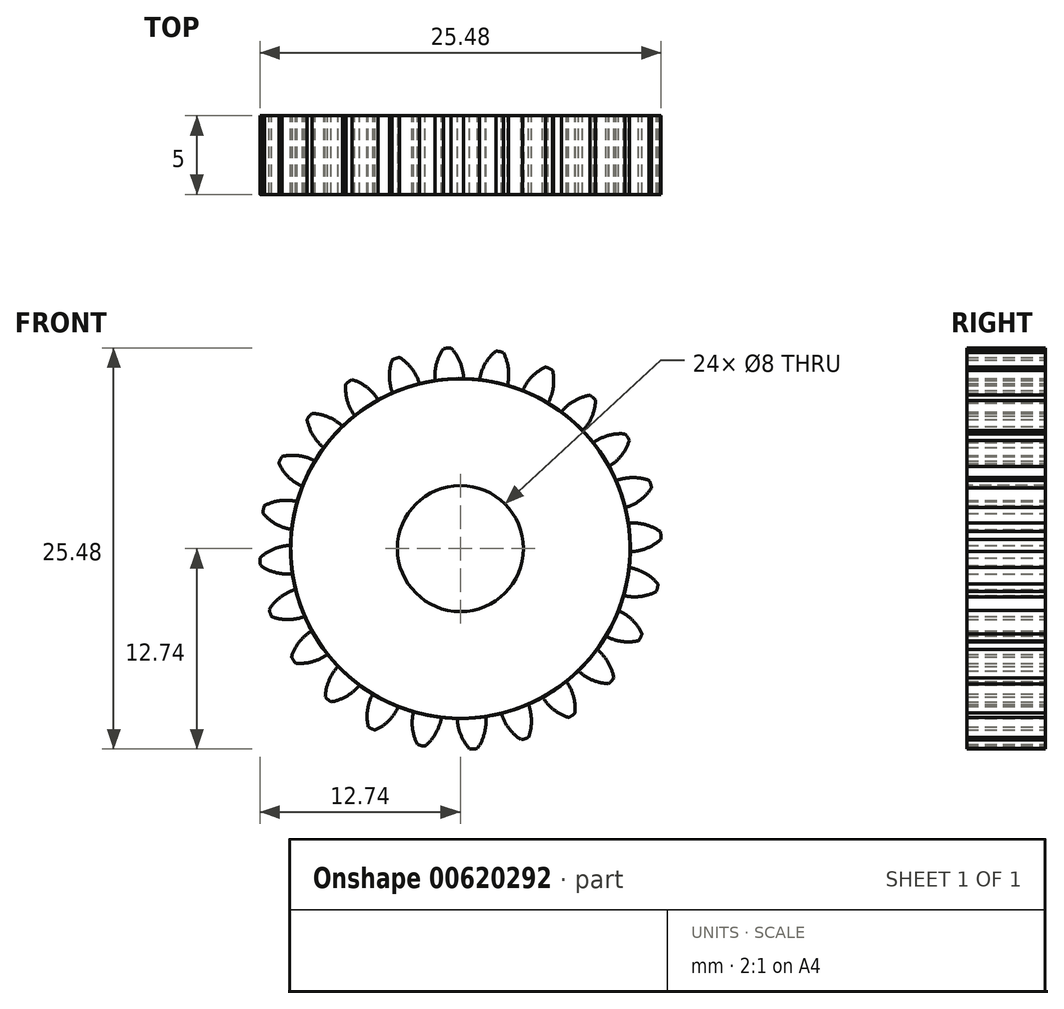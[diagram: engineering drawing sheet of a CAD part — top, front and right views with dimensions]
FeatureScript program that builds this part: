
annotation { "Feature Type Name" : "Feature", "Feature Type Description" : "" }
export const myFeature = defineFeature(function(context is Context, id is Id, definition is map)
    precondition{}
    {
        {
            var Q0;
            Q0=qCreatedBy(makeId("Front.planeOp"),FACE);
            var sketch = newSketch(context, id + "F0", { "sketchPlane" : qUnion([Q0])});
            skCircle(sketch, "E0", {"center": v(0, 0) * mm, "radius": 6.34 * mm});
            skCircle(sketch, "E1", {"center": v(0, 0) * mm, "radius": 6.93 * mm, "construction": true});
            skCircle(sketch, "E2", {"center": v(0, 0) * mm, "radius": 7.5 * mm, "construction": true});
            skLineSegment(sketch, "E3", {"start": v(0, 0) * mm, "end": v(0, 11.09) * mm, "construction": true});
            skLineSegment(sketch, "E4", {"start": v(0, 0) * mm, "end": v(-0.73, 11.09) * mm, "construction": true});
            skLineSegment(sketch, "E5", {"start": v(0, 6.93) * mm, "end": v(-9.56, 6.93) * mm, "construction": true});
            skLineSegment(sketch, "E6", {"start": v(0, 6.93) * mm, "end": v(-10.36, 3.16) * mm, "construction": true});
            skCircle(sketch, "E7", {"center": v(0, 6.93) * mm, "radius": 1.73 * mm, "construction": true});
            skCircle(sketch, "E8", {"center": v(0, 0) * mm, "radius": 6.51 * mm, "construction": true});
            skCircle(sketch, "E9", {"center": v(-1.6, 6.31) * mm, "radius": 1.73 * mm, "construction": true});
            skArc(sketch, "E10", {"start": v(0, 6.93) * mm, "mid": v(-0.15, 7.22) * mm, "end": v(-0.35, 7.49) * mm});
            skArc(sketch, "E11", {"start": v(0.12, 6.34) * mm, "mid": v(0.08, 6.64) * mm, "end": v(0, 6.93) * mm});
            skArc(sketch, "E12.MirrorCS", {"start": v(-0.9, 6.87) * mm, "mid": v(-0.8, 7.18) * mm, "end": v(-0.63, 7.47) * mm});
            skArc(sketch, "E13.MirrorCS", {"start": v(-0.94, 6.27) * mm, "mid": v(-0.95, 6.57) * mm, "end": v(-0.9, 6.87) * mm});
            skArc(sketch, "E14", {"start": v(-0.35, 7.49) * mm, "mid": v(-0.5, 7.5) * mm, "end": v(-0.63, 7.47) * mm});
            skSolve(sketch);
        }
        {
            var Q0;
            {var subQ0=sQuery(id+"F0.wireOp",EDGE,"E0");var subQ1=makeQuery(id+"F0.imprint","INTERSECT",VERTEX,{"derivedFrom":[subQ0,sQuery(id+"F0.wireOp",EDGE,"E11")]});Q0=makeQuery(id+"F0.imprint","IMPRINT",FACE,{"disambiguationData":[TD([[makeQuery(id+"F0.imprint","IMPRINT",EDGE,{"disambiguationData":[TD([[subQ1,-1.0]])],"derivedFrom":subQ0}),1.0]])]});}
            var Q1;
            Q1=makeQuery(id+"F0.imprint","IMPRINT",FACE,{"disambiguationData":[TD([[makeQuery(id+"F0.imprint","IMPRINT",EDGE,{"derivedFrom":sQuery(id+"F0.wireOp",EDGE,"E10")}),1.0]])]});
            extrude(context, id + "F1", {"entities" : qUnion([Q0, Q1]), "depth" : 2.94 * mm, "offsetDistance" : 25 * mm});
        }
        {
            var Q0;
            Q0=makeQuery(id+"F1.opExtrude","SWEPT_BODY",BODY,{"disambiguationData":[OSD([sQuery(id+"F0.wireOp",EDGE,"E0"),sQuery(id+"F0.wireOp",EDGE,"E10"),sQuery(id+"F0.wireOp",EDGE,"E11"),sQuery(id+"F0.wireOp",EDGE,"E12.MirrorCS"),sQuery(id+"F0.wireOp",EDGE,"E13.MirrorCS"),sQuery(id+"F0.wireOp",EDGE,"E14")])]});
            var Q1;
            Q1=makeQuery(id+"F1.opExtrude","SWEPT_FACE",FACE,{"disambiguationData":[OSD([sQuery(id+"F0.wireOp",EDGE,"E0")])]});
            circularPattern(context, id + "F2", {"entities" : qUnion([Q0]), "axis" : qUnion([Q1]), "angle" : 360 * degree, "instanceCount" : 24, "equalSpace" : true});
        }
        {
            var Q0;
            Q0=makeQuery(id+"F2.opPattern","COPY",FACE,{"derivedFrom":makeQuery(id+"F1.opExtrude","CAP_FACE",FACE,{"disambiguationData":[OSD([sQuery(id+"F0.wireOp",EDGE,"E0"),sQuery(id+"F0.wireOp",EDGE,"E10"),sQuery(id+"F0.wireOp",EDGE,"E11"),sQuery(id+"F0.wireOp",EDGE,"E12.MirrorCS"),sQuery(id+"F0.wireOp",EDGE,"E13.MirrorCS"),sQuery(id+"F0.wireOp",EDGE,"E14")])],"isStart":false}),"instanceName":"3"});
            var sketch = newSketch(context, id + "F3", { "sketchPlane" : qUnion([Q0])});
            skCircle(sketch, "E15", {"center": v(0, 0) * mm, "radius": 2.35 * mm});
            skSolve(sketch);
        }
        {
            var Q0;
            Q0=qSketchRegion(id+"F3",true);
            extrude(context, id + "F4", {"entities" : qUnion([Q0]), "operationType" : NewBodyOperationType.REMOVE, "endBound" : BoundingType.UP_TO_NEXT, "oppositeDirection" : true, "depth" : 25 * mm, "offsetDistance" : 25 * mm});
        }
        {
            var Q0;
            Q0=makeQuery(id+"F2.opPattern","COPY",BODY,{"derivedFrom":makeQuery(id+"F1.opExtrude","SWEPT_BODY",BODY,{"disambiguationData":[OSD([sQuery(id+"F0.wireOp",EDGE,"E0"),sQuery(id+"F0.wireOp",EDGE,"E10"),sQuery(id+"F0.wireOp",EDGE,"E11"),sQuery(id+"F0.wireOp",EDGE,"E12.MirrorCS"),sQuery(id+"F0.wireOp",EDGE,"E13.MirrorCS"),sQuery(id+"F0.wireOp",EDGE,"E14")])]}),"instanceName":"23"});
            var Q1;
            Q1=makeQuery(id+"F2.opPattern","COPY",BODY,{"derivedFrom":makeQuery(id+"F1.opExtrude","SWEPT_BODY",BODY,{"disambiguationData":[OSD([sQuery(id+"F0.wireOp",EDGE,"E0"),sQuery(id+"F0.wireOp",EDGE,"E10"),sQuery(id+"F0.wireOp",EDGE,"E11"),sQuery(id+"F0.wireOp",EDGE,"E12.MirrorCS"),sQuery(id+"F0.wireOp",EDGE,"E13.MirrorCS"),sQuery(id+"F0.wireOp",EDGE,"E14")])]}),"instanceName":"11"});
            var Q2;
            Q2=makeQuery(id+"F2.opPattern","COPY",BODY,{"derivedFrom":makeQuery(id+"F1.opExtrude","SWEPT_BODY",BODY,{"disambiguationData":[OSD([sQuery(id+"F0.wireOp",EDGE,"E0"),sQuery(id+"F0.wireOp",EDGE,"E10"),sQuery(id+"F0.wireOp",EDGE,"E11"),sQuery(id+"F0.wireOp",EDGE,"E12.MirrorCS"),sQuery(id+"F0.wireOp",EDGE,"E13.MirrorCS"),sQuery(id+"F0.wireOp",EDGE,"E14")])]}),"instanceName":"12"});
            var Q3;
            Q3=makeQuery(id+"F2.opPattern","COPY",BODY,{"derivedFrom":makeQuery(id+"F1.opExtrude","SWEPT_BODY",BODY,{"disambiguationData":[OSD([sQuery(id+"F0.wireOp",EDGE,"E0"),sQuery(id+"F0.wireOp",EDGE,"E10"),sQuery(id+"F0.wireOp",EDGE,"E11"),sQuery(id+"F0.wireOp",EDGE,"E12.MirrorCS"),sQuery(id+"F0.wireOp",EDGE,"E13.MirrorCS"),sQuery(id+"F0.wireOp",EDGE,"E14")])]}),"instanceName":"3"});
            var Q4;
            Q4=makeQuery(id+"F2.opPattern","COPY",BODY,{"derivedFrom":makeQuery(id+"F1.opExtrude","SWEPT_BODY",BODY,{"disambiguationData":[OSD([sQuery(id+"F0.wireOp",EDGE,"E0"),sQuery(id+"F0.wireOp",EDGE,"E10"),sQuery(id+"F0.wireOp",EDGE,"E11"),sQuery(id+"F0.wireOp",EDGE,"E12.MirrorCS"),sQuery(id+"F0.wireOp",EDGE,"E13.MirrorCS"),sQuery(id+"F0.wireOp",EDGE,"E14")])]}),"instanceName":"13"});
            var Q5;
            Q5=makeQuery(id+"F2.opPattern","COPY",BODY,{"derivedFrom":makeQuery(id+"F1.opExtrude","SWEPT_BODY",BODY,{"disambiguationData":[OSD([sQuery(id+"F0.wireOp",EDGE,"E0"),sQuery(id+"F0.wireOp",EDGE,"E10"),sQuery(id+"F0.wireOp",EDGE,"E11"),sQuery(id+"F0.wireOp",EDGE,"E12.MirrorCS"),sQuery(id+"F0.wireOp",EDGE,"E13.MirrorCS"),sQuery(id+"F0.wireOp",EDGE,"E14")])]}),"instanceName":"7"});
            var Q6;
            Q6=makeQuery(id+"F2.opPattern","COPY",BODY,{"derivedFrom":makeQuery(id+"F1.opExtrude","SWEPT_BODY",BODY,{"disambiguationData":[OSD([sQuery(id+"F0.wireOp",EDGE,"E0"),sQuery(id+"F0.wireOp",EDGE,"E10"),sQuery(id+"F0.wireOp",EDGE,"E11"),sQuery(id+"F0.wireOp",EDGE,"E12.MirrorCS"),sQuery(id+"F0.wireOp",EDGE,"E13.MirrorCS"),sQuery(id+"F0.wireOp",EDGE,"E14")])]}),"instanceName":"8"});
            var Q7;
            Q7=makeQuery(id+"F2.opPattern","COPY",BODY,{"derivedFrom":makeQuery(id+"F1.opExtrude","SWEPT_BODY",BODY,{"disambiguationData":[OSD([sQuery(id+"F0.wireOp",EDGE,"E0"),sQuery(id+"F0.wireOp",EDGE,"E10"),sQuery(id+"F0.wireOp",EDGE,"E11"),sQuery(id+"F0.wireOp",EDGE,"E12.MirrorCS"),sQuery(id+"F0.wireOp",EDGE,"E13.MirrorCS"),sQuery(id+"F0.wireOp",EDGE,"E14")])]}),"instanceName":"1"});
            var Q8;
            Q8=makeQuery(id+"F2.opPattern","COPY",BODY,{"derivedFrom":makeQuery(id+"F1.opExtrude","SWEPT_BODY",BODY,{"disambiguationData":[OSD([sQuery(id+"F0.wireOp",EDGE,"E0"),sQuery(id+"F0.wireOp",EDGE,"E10"),sQuery(id+"F0.wireOp",EDGE,"E11"),sQuery(id+"F0.wireOp",EDGE,"E12.MirrorCS"),sQuery(id+"F0.wireOp",EDGE,"E13.MirrorCS"),sQuery(id+"F0.wireOp",EDGE,"E14")])]}),"instanceName":"14"});
            var Q9;
            Q9=makeQuery(id+"F2.opPattern","COPY",BODY,{"derivedFrom":makeQuery(id+"F1.opExtrude","SWEPT_BODY",BODY,{"disambiguationData":[OSD([sQuery(id+"F0.wireOp",EDGE,"E0"),sQuery(id+"F0.wireOp",EDGE,"E10"),sQuery(id+"F0.wireOp",EDGE,"E11"),sQuery(id+"F0.wireOp",EDGE,"E12.MirrorCS"),sQuery(id+"F0.wireOp",EDGE,"E13.MirrorCS"),sQuery(id+"F0.wireOp",EDGE,"E14")])]}),"instanceName":"21"});
            var Q10;
            Q10=makeQuery(id+"F2.opPattern","COPY",BODY,{"derivedFrom":makeQuery(id+"F1.opExtrude","SWEPT_BODY",BODY,{"disambiguationData":[OSD([sQuery(id+"F0.wireOp",EDGE,"E0"),sQuery(id+"F0.wireOp",EDGE,"E10"),sQuery(id+"F0.wireOp",EDGE,"E11"),sQuery(id+"F0.wireOp",EDGE,"E12.MirrorCS"),sQuery(id+"F0.wireOp",EDGE,"E13.MirrorCS"),sQuery(id+"F0.wireOp",EDGE,"E14")])]}),"instanceName":"9"});
            var Q11;
            Q11=makeQuery(id+"F2.opPattern","COPY",BODY,{"derivedFrom":makeQuery(id+"F1.opExtrude","SWEPT_BODY",BODY,{"disambiguationData":[OSD([sQuery(id+"F0.wireOp",EDGE,"E0"),sQuery(id+"F0.wireOp",EDGE,"E10"),sQuery(id+"F0.wireOp",EDGE,"E11"),sQuery(id+"F0.wireOp",EDGE,"E12.MirrorCS"),sQuery(id+"F0.wireOp",EDGE,"E13.MirrorCS"),sQuery(id+"F0.wireOp",EDGE,"E14")])]}),"instanceName":"2"});
            var Q12;
            Q12=makeQuery(id+"F1.opExtrude","SWEPT_BODY",BODY,{"disambiguationData":[OSD([sQuery(id+"F0.wireOp",EDGE,"E0"),sQuery(id+"F0.wireOp",EDGE,"E10"),sQuery(id+"F0.wireOp",EDGE,"E11"),sQuery(id+"F0.wireOp",EDGE,"E12.MirrorCS"),sQuery(id+"F0.wireOp",EDGE,"E13.MirrorCS"),sQuery(id+"F0.wireOp",EDGE,"E14")])]});
            var Q13;
            Q13=makeQuery(id+"F2.opPattern","COPY",BODY,{"derivedFrom":makeQuery(id+"F1.opExtrude","SWEPT_BODY",BODY,{"disambiguationData":[OSD([sQuery(id+"F0.wireOp",EDGE,"E0"),sQuery(id+"F0.wireOp",EDGE,"E10"),sQuery(id+"F0.wireOp",EDGE,"E11"),sQuery(id+"F0.wireOp",EDGE,"E12.MirrorCS"),sQuery(id+"F0.wireOp",EDGE,"E13.MirrorCS"),sQuery(id+"F0.wireOp",EDGE,"E14")])]}),"instanceName":"22"});
            var Q14;
            Q14=makeQuery(id+"F2.opPattern","COPY",BODY,{"derivedFrom":makeQuery(id+"F1.opExtrude","SWEPT_BODY",BODY,{"disambiguationData":[OSD([sQuery(id+"F0.wireOp",EDGE,"E0"),sQuery(id+"F0.wireOp",EDGE,"E10"),sQuery(id+"F0.wireOp",EDGE,"E11"),sQuery(id+"F0.wireOp",EDGE,"E12.MirrorCS"),sQuery(id+"F0.wireOp",EDGE,"E13.MirrorCS"),sQuery(id+"F0.wireOp",EDGE,"E14")])]}),"instanceName":"4"});
            var Q15;
            Q15=makeQuery(id+"F2.opPattern","COPY",BODY,{"derivedFrom":makeQuery(id+"F1.opExtrude","SWEPT_BODY",BODY,{"disambiguationData":[OSD([sQuery(id+"F0.wireOp",EDGE,"E0"),sQuery(id+"F0.wireOp",EDGE,"E10"),sQuery(id+"F0.wireOp",EDGE,"E11"),sQuery(id+"F0.wireOp",EDGE,"E12.MirrorCS"),sQuery(id+"F0.wireOp",EDGE,"E13.MirrorCS"),sQuery(id+"F0.wireOp",EDGE,"E14")])]}),"instanceName":"16"});
            var Q16;
            Q16=makeQuery(id+"F2.opPattern","COPY",BODY,{"derivedFrom":makeQuery(id+"F1.opExtrude","SWEPT_BODY",BODY,{"disambiguationData":[OSD([sQuery(id+"F0.wireOp",EDGE,"E0"),sQuery(id+"F0.wireOp",EDGE,"E10"),sQuery(id+"F0.wireOp",EDGE,"E11"),sQuery(id+"F0.wireOp",EDGE,"E12.MirrorCS"),sQuery(id+"F0.wireOp",EDGE,"E13.MirrorCS"),sQuery(id+"F0.wireOp",EDGE,"E14")])]}),"instanceName":"10"});
            var Q17;
            Q17=makeQuery(id+"F2.opPattern","COPY",BODY,{"derivedFrom":makeQuery(id+"F1.opExtrude","SWEPT_BODY",BODY,{"disambiguationData":[OSD([sQuery(id+"F0.wireOp",EDGE,"E0"),sQuery(id+"F0.wireOp",EDGE,"E10"),sQuery(id+"F0.wireOp",EDGE,"E11"),sQuery(id+"F0.wireOp",EDGE,"E12.MirrorCS"),sQuery(id+"F0.wireOp",EDGE,"E13.MirrorCS"),sQuery(id+"F0.wireOp",EDGE,"E14")])]}),"instanceName":"17"});
            var Q18;
            Q18=makeQuery(id+"F2.opPattern","COPY",BODY,{"derivedFrom":makeQuery(id+"F1.opExtrude","SWEPT_BODY",BODY,{"disambiguationData":[OSD([sQuery(id+"F0.wireOp",EDGE,"E0"),sQuery(id+"F0.wireOp",EDGE,"E10"),sQuery(id+"F0.wireOp",EDGE,"E11"),sQuery(id+"F0.wireOp",EDGE,"E12.MirrorCS"),sQuery(id+"F0.wireOp",EDGE,"E13.MirrorCS"),sQuery(id+"F0.wireOp",EDGE,"E14")])]}),"instanceName":"15"});
            var Q19;
            Q19=makeQuery(id+"F2.opPattern","COPY",BODY,{"derivedFrom":makeQuery(id+"F1.opExtrude","SWEPT_BODY",BODY,{"disambiguationData":[OSD([sQuery(id+"F0.wireOp",EDGE,"E0"),sQuery(id+"F0.wireOp",EDGE,"E10"),sQuery(id+"F0.wireOp",EDGE,"E11"),sQuery(id+"F0.wireOp",EDGE,"E12.MirrorCS"),sQuery(id+"F0.wireOp",EDGE,"E13.MirrorCS"),sQuery(id+"F0.wireOp",EDGE,"E14")])]}),"instanceName":"5"});
            var Q20;
            Q20=makeQuery(id+"F2.opPattern","COPY",BODY,{"derivedFrom":makeQuery(id+"F1.opExtrude","SWEPT_BODY",BODY,{"disambiguationData":[OSD([sQuery(id+"F0.wireOp",EDGE,"E0"),sQuery(id+"F0.wireOp",EDGE,"E10"),sQuery(id+"F0.wireOp",EDGE,"E11"),sQuery(id+"F0.wireOp",EDGE,"E12.MirrorCS"),sQuery(id+"F0.wireOp",EDGE,"E13.MirrorCS"),sQuery(id+"F0.wireOp",EDGE,"E14")])]}),"instanceName":"6"});
            var Q21;
            Q21=makeQuery(id+"F2.opPattern","COPY",BODY,{"derivedFrom":makeQuery(id+"F1.opExtrude","SWEPT_BODY",BODY,{"disambiguationData":[OSD([sQuery(id+"F0.wireOp",EDGE,"E0"),sQuery(id+"F0.wireOp",EDGE,"E10"),sQuery(id+"F0.wireOp",EDGE,"E11"),sQuery(id+"F0.wireOp",EDGE,"E12.MirrorCS"),sQuery(id+"F0.wireOp",EDGE,"E13.MirrorCS"),sQuery(id+"F0.wireOp",EDGE,"E14")])]}),"instanceName":"20"});
            var Q22;
            Q22=makeQuery(id+"F2.opPattern","COPY",BODY,{"derivedFrom":makeQuery(id+"F1.opExtrude","SWEPT_BODY",BODY,{"disambiguationData":[OSD([sQuery(id+"F0.wireOp",EDGE,"E0"),sQuery(id+"F0.wireOp",EDGE,"E10"),sQuery(id+"F0.wireOp",EDGE,"E11"),sQuery(id+"F0.wireOp",EDGE,"E12.MirrorCS"),sQuery(id+"F0.wireOp",EDGE,"E13.MirrorCS"),sQuery(id+"F0.wireOp",EDGE,"E14")])]}),"instanceName":"19"});
            var Q23;
            Q23=makeQuery(id+"F2.opPattern","COPY",BODY,{"derivedFrom":makeQuery(id+"F1.opExtrude","SWEPT_BODY",BODY,{"disambiguationData":[OSD([sQuery(id+"F0.wireOp",EDGE,"E0"),sQuery(id+"F0.wireOp",EDGE,"E10"),sQuery(id+"F0.wireOp",EDGE,"E11"),sQuery(id+"F0.wireOp",EDGE,"E12.MirrorCS"),sQuery(id+"F0.wireOp",EDGE,"E13.MirrorCS"),sQuery(id+"F0.wireOp",EDGE,"E14")])]}),"instanceName":"18"});
            var Q24;
            Q24=sQuery(id+"F0.wireOp",VERTEX,"E0.center");
            transform(context, id + "F5", {"entities" : qUnion([Q0, Q1, Q2, Q3, Q4, Q5, Q6, Q7, Q8, Q9, Q10, Q11, Q12, Q13, Q14, Q15, Q16, Q17, Q18, Q19, Q20, Q21, Q22, Q23]), "transformType" : TransformType.SCALE_UNIFORMLY, "scale" : 1.7, "scalePoint" : qUnion([Q24]), "makeCopy" : false});
        }
    });
